# Revit family: SWF-P
name_source: partatom
category: Air Terminals
revit_build: Autodesk Revit MEP 2012 (Build: 20110309_2315(x64)
units: mm (PartAtom-declared; Revit-internal decimal feet)

## types (5) — shared parameters
Alto = 13 13/16"
Alto perfil = 1 9/16"
Alto placa = 1/8"
B plato = 22 1/8"
Cuello = Redondo
Diametro int = 5 7/8"
Espesor = 21 15/16"
Largo superior = 23 21/32"
Manufacturer = INNES
Material = Acero
Máxima velocidad de cuello = 1100 FPM
Mínima velocidad de cuello = 200 FPM
Radio int = 2 15/16"
URL = http://www.innes.com

## per-type parameters (varying)
| type | Diametro | Max Flow | Min Flow | Máxima presión total | Máximo nivel de ruido (NC) | Mínima presión total | Radio |
| SWF-P-06 | 6" | 216 CFM | 6 CFM | 0.16 in-wg | 30 | 0.00 in-wg | 3" |
| SWF-P-08 | 8" | 384 CFM | 70 CFM | 0.22 in-wg | 40 | 0.01 in-wg | 4" |
| SWF-P-10 | 10" | 601 CFM | 109 CFM | 0.36 in-wg | 44 | 0.01 in-wg | 5" |
| SWF-P-12 | 12" | 864 CFM | 157 CFM | 0.67 in-wg | 51 | 0.02 in-wg | 6" |
| SWF-P-14 | 14" | 1127 CFM | 205 CFM | 0.98 in-wg | 58 | 0.04 in-wg | 7" |

## geometry (parser evidence)
native form markers: Sweep x4
no freeform markers — native parametric forms only
